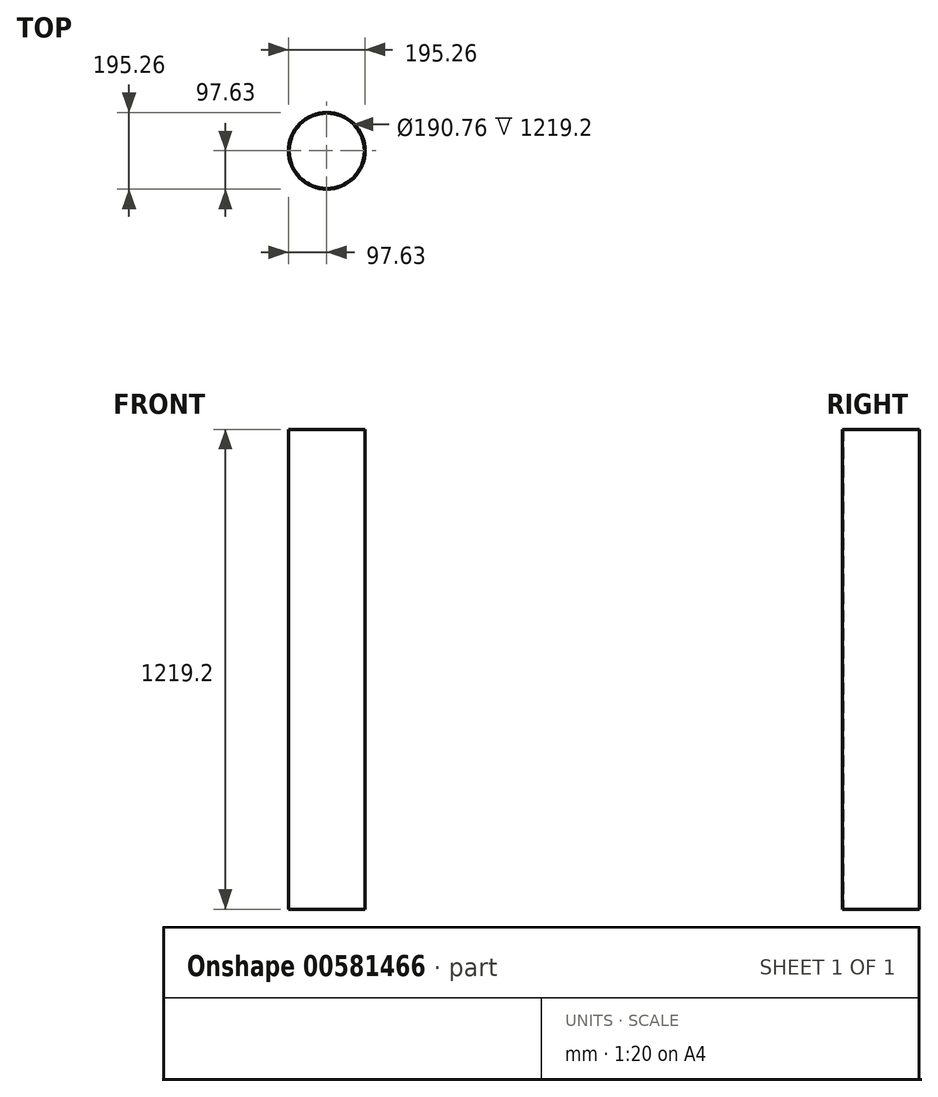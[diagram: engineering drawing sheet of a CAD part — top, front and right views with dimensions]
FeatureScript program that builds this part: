
annotation { "Feature Type Name" : "Feature", "Feature Type Description" : "" }
export const myFeature = defineFeature(function(context is Context, id is Id, definition is map)
    precondition{}
    {
        {
            var Q0;
            Q0=qCreatedBy(makeId("Top.planeOp"),FACE);
            var sketch = newSketch(context, id + "F0", { "sketchPlane" : qUnion([Q0])});
            skCircle(sketch, "E0", {"center": v(0, 0) * mm, "radius": 97.63 * mm});
            skCircle(sketch, "E1", {"center": v(0, 0) * mm, "radius": 95.38 * mm});
            skSolve(sketch);
        }
        {
            var Q0;
            Q0=makeQuery(id+"F0.imprint","IMPRINT",FACE,{"disambiguationData":[TD([[makeQuery(id+"F0.imprint","IMPRINT",EDGE,{"derivedFrom":sQuery(id+"F0.wireOp",EDGE,"E0")}),1.0]])]});
            extrude(context, id + "F1", {"entities" : qUnion([Q0]), "depth" : 1219.2 * mm, "offsetDistance" : 25 * mm});
        }
    });
